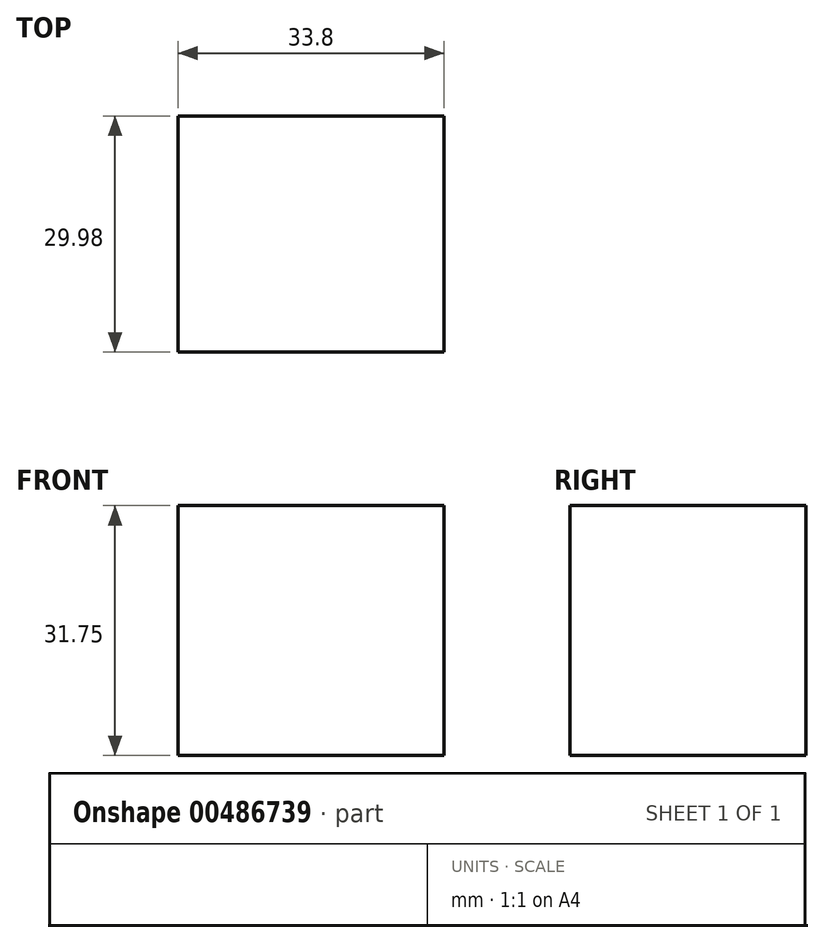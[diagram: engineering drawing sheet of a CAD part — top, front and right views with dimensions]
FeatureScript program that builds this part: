
annotation { "Feature Type Name" : "Feature", "Feature Type Description" : "" }
export const myFeature = defineFeature(function(context is Context, id is Id, definition is map)
    precondition{}
    {
        {
            var Q0;
            Q0=qCreatedBy(makeId("Top.planeOp"),FACE);
            var sketch = newSketch(context, id + "F0", { "sketchPlane" : qUnion([Q0])});
            skLineSegment(sketch, "E0.bottom", {"start": v(16.9, 15) * mm, "end": v(-16.9, 15) * mm});
            skLineSegment(sketch, "E0.top", {"start": v(16.9, -15) * mm, "end": v(-16.9, -15) * mm});
            skLineSegment(sketch, "E0.left", {"start": v(16.9, 15) * mm, "end": v(16.9, -15) * mm});
            skLineSegment(sketch, "E0.right", {"start": v(-16.9, 15) * mm, "end": v(-16.9, -15) * mm});
            skPoint(sketch, "E0.middle", {"position": v(0, 0) * mm});
            skSolve(sketch);
        }
        {
            var Q0;
            Q0=makeQuery(id+"F0.imprint","IMPRINT",FACE,{"disambiguationData":[TD([[makeQuery(id+"F0.imprint","IMPRINT",EDGE,{"derivedFrom":sQuery(id+"F0.wireOp",EDGE,"E0.bottom")}),1.0]])]});
            extrude(context, id + "F1", {"entities" : qUnion([Q0]), "depth" : 31.75 * mm});
        }
    });
